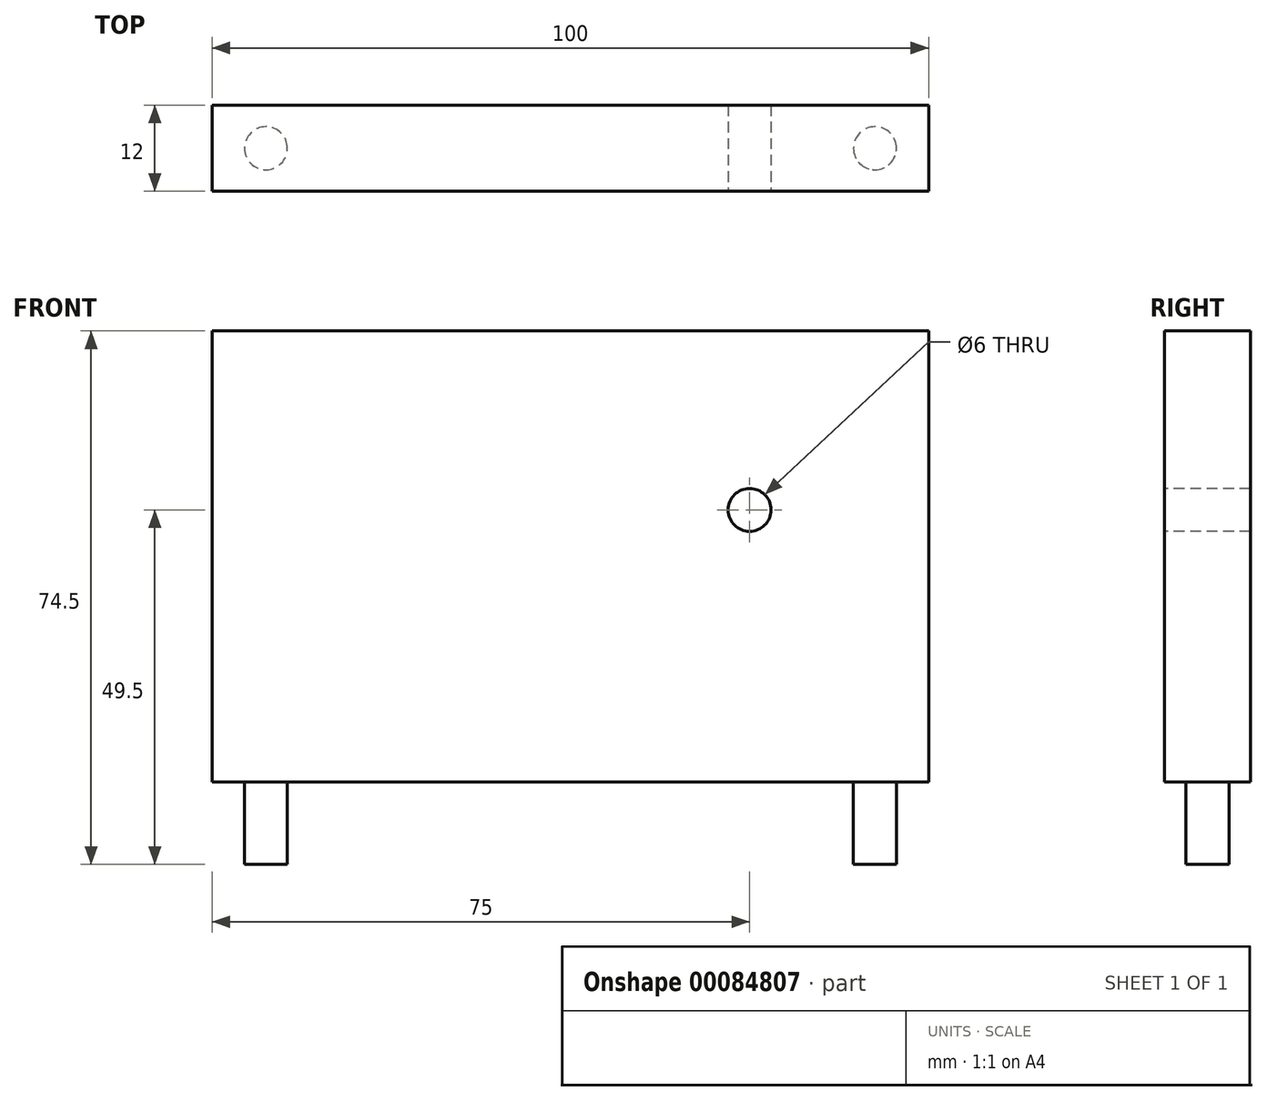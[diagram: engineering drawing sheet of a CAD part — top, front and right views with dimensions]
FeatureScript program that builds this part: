
annotation { "Feature Type Name" : "Feature", "Feature Type Description" : "" }
export const myFeature = defineFeature(function(context is Context, id is Id, definition is map)
    precondition{}
    {
        {
            var Q0;
            Q0=qCreatedBy(makeId("Front.planeOp"),FACE);
            var sketch = newSketch(context, id + "F0", { "sketchPlane" : qUnion([Q0])});
            skLineSegment(sketch, "E0.bottom", {"start": v(0, 0) * mm, "end": v(100, 0) * mm});
            skLineSegment(sketch, "E0.top", {"start": v(0, 63) * mm, "end": v(100, 63) * mm});
            skLineSegment(sketch, "E0.left", {"start": v(0, 0) * mm, "end": v(0, 63) * mm});
            skLineSegment(sketch, "E0.right", {"start": v(100, 0) * mm, "end": v(100, 63) * mm});
            skSolve(sketch);
        }
        {
            var Q0;
            Q0 = qSketchRegion(id + "F0", true);
            extrude(context, id + "F1", {"entities" : qUnion([Q0]), "depth" : 12 * mm});
        }
        {
            var Q0;
            Q0=makeQuery(id+"F1.opExtrude","SWEPT_FACE",FACE,{"disambiguationData":[OSD([sQuery(id+"F0.wireOp",EDGE,"E0.bottom")])]});
            var sketch = newSketch(context, id + "F2", { "sketchPlane" : qUnion([Q0])});
            skLineSegment(sketch, "E1", {"start": v(0, 6) * mm, "end": v(100, 6) * mm, "construction": true});
            skCircle(sketch, "E2", {"center": v(7.5, 6) * mm, "radius": 3 * mm});
            skCircle(sketch, "E3", {"center": v(92.5, 6) * mm, "radius": 3 * mm});
            skLineSegment(sketch, "E4", {"start": v(50, 12) * mm, "end": v(50, 0) * mm, "construction": true});
            skLineSegment(sketch, "E5", {"start": v(7.5, 6) * mm, "end": v(92.5, 6) * mm, "construction": true});
            skLineSegment(sketch, "E6", {"start": v(50, 6) * mm, "end": v(50, 12) * mm, "construction": true});
            skSolve(sketch);
        }
        {
            var Q0;
            Q0 = qSketchRegion(id + "F2", true);
            extrude(context, id + "F3", {"entities" : qUnion([Q0]), "operationType" : NewBodyOperationType.ADD, "depth" : 11.5 * mm});
        }
        {
            var Q0;
            Q0=makeQuery(id+"F1.opExtrude","CAP_FACE",FACE,{"disambiguationData":[OSD([sQuery(id+"F0.wireOp",EDGE,"E0.bottom"),sQuery(id+"F0.wireOp",EDGE,"E0.top"),sQuery(id+"F0.wireOp",EDGE,"E0.left"),sQuery(id+"F0.wireOp",EDGE,"E0.right")])],"isStart":false});
            var sketch = newSketch(context, id + "F4", { "sketchPlane" : qUnion([Q0])});
            skCircle(sketch, "E7", {"center": v(75, 38) * mm, "radius": 3 * mm});
            skLineSegment(sketch, "E8", {"start": v(50, 0) * mm, "end": v(50, 63) * mm, "construction": true});
            skSolve(sketch);
        }
        {
            var Q0;
            Q0 = qSketchRegion(id + "F4", true);
            extrude(context, id + "F5", {"entities" : qUnion([Q0]), "operationType" : NewBodyOperationType.REMOVE, "endBound" : BoundingType.THROUGH_ALL, "oppositeDirection" : true, "depth" : 25 * mm});
        }
    });
